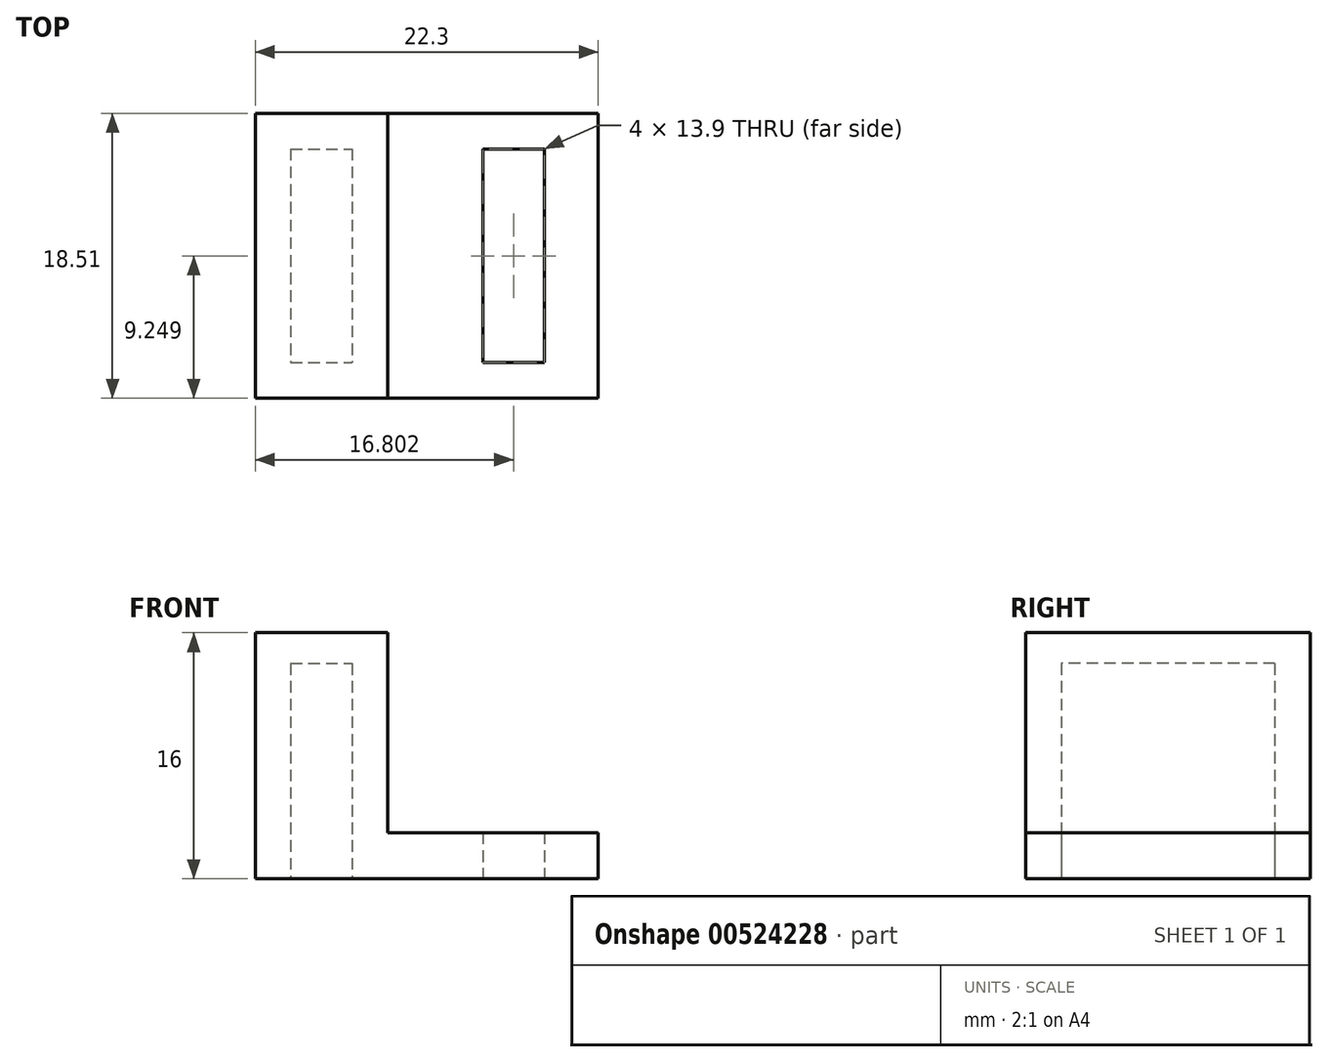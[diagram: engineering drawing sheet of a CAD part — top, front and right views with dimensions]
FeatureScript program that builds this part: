
annotation { "Feature Type Name" : "Feature", "Feature Type Description" : "" }
export const myFeature = defineFeature(function(context is Context, id is Id, definition is map)
    precondition{}
    {
        {
            var Q0;
            Q0=qCreatedBy(makeId("Top.planeOp"),FACE);
            var sketch = newSketch(context, id + "F0", { "sketchPlane" : qUnion([Q0])});
            skLineSegment(sketch, "E0.bottom", {"start": v(-48.96, 30.49) * mm, "end": v(-44.96, 30.49) * mm});
            skLineSegment(sketch, "E0.top", {"start": v(-48.96, 16.59) * mm, "end": v(-44.96, 16.59) * mm});
            skLineSegment(sketch, "E0.left", {"start": v(-48.96, 30.49) * mm, "end": v(-48.96, 16.59) * mm});
            skLineSegment(sketch, "E0.right", {"start": v(-44.96, 30.49) * mm, "end": v(-44.96, 16.59) * mm});
            skLineSegment(sketch, "E1", {"start": v(-44.96, 22.44) * mm, "end": v(-42.66, 22.44) * mm, "construction": true});
            skLineSegment(sketch, "E2", {"start": v(-42.66, 22.44) * mm, "end": v(-42.66, 42.18) * mm, "construction": true});
            skLineSegment(sketch, "E3", {"start": v(-42.66, 42.18) * mm, "end": v(-42.66, 0) * mm, "construction": true});
            skLineSegment(sketch, "E4", {"start": v(-46.96, 30.49) * mm, "end": v(-46.96, 32.79) * mm, "construction": true});
            skLineSegment(sketch, "E5", {"start": v(-46.96, 16.59) * mm, "end": v(-46.96, 14.29) * mm, "construction": true});
            skLineSegment(sketch, "E6", {"start": v(-42.66, 37.35) * mm, "end": v(-28.96, 37.35) * mm, "construction": true});
            skLineSegment(sketch, "E7", {"start": v(-28.96, 37.35) * mm, "end": v(-28.96, 6.43) * mm, "construction": true});
            skLineSegment(sketch, "E8", {"start": v(-46.96, 14.29) * mm, "end": v(-20.97, 14.29) * mm, "construction": true});
            skLineSegment(sketch, "E9", {"start": v(-48.96, 23.54) * mm, "end": v(-51.26, 23.54) * mm, "construction": true});
            skLineSegment(sketch, "E10", {"start": v(-51.26, 23.54) * mm, "end": v(-51.26, 42.06) * mm, "construction": true});
            skLineSegment(sketch, "E11", {"start": v(-51.26, 42.06) * mm, "end": v(-51.26, -3.78) * mm, "construction": true});
            skLineSegment(sketch, "E12", {"start": v(-46.96, 14.29) * mm, "end": v(-58.37, 14.29) * mm, "construction": true});
            skLineSegment(sketch, "E13.bottom", {"start": v(-51.26, 32.8) * mm, "end": v(-28.96, 32.8) * mm});
            skLineSegment(sketch, "E13.top", {"start": v(-51.26, 14.29) * mm, "end": v(-28.96, 14.29) * mm});
            skLineSegment(sketch, "E13.left", {"start": v(-51.26, 32.8) * mm, "end": v(-51.26, 14.29) * mm});
            skLineSegment(sketch, "E13.right", {"start": v(-28.96, 32.8) * mm, "end": v(-28.96, 14.29) * mm});
            skLineSegment(sketch, "E14", {"start": v(-44.96, 30.49) * mm, "end": v(-22.07, 30.49) * mm, "construction": true});
            skLineSegment(sketch, "E15", {"start": v(-44.96, 16.59) * mm, "end": v(-20.97, 16.59) * mm, "construction": true});
            skLineSegment(sketch, "E16", {"start": v(-28.96, 6.43) * mm, "end": v(-32.46, 6.43) * mm, "construction": true});
            skLineSegment(sketch, "E17", {"start": v(-32.46, 6.43) * mm, "end": v(-32.46, 38.78) * mm, "construction": true});
            skPoint(sketch, "E18.firstSnap0", {"position": v(-32.97, 16.59) * mm});
            skLineSegment(sketch, "E18.bottom", {"start": v(-32.46, 16.59) * mm, "end": v(-36.46, 16.59) * mm});
            skLineSegment(sketch, "E18.top", {"start": v(-32.46, 30.49) * mm, "end": v(-36.46, 30.49) * mm});
            skLineSegment(sketch, "E18.left", {"start": v(-32.46, 16.59) * mm, "end": v(-32.46, 30.49) * mm});
            skLineSegment(sketch, "E18.right", {"start": v(-36.46, 16.59) * mm, "end": v(-36.46, 30.49) * mm});
            skLineSegment(sketch, "E19", {"start": v(-42.66, 32.8) * mm, "end": v(-42.66, 14.29) * mm});
            skSolve(sketch);
        }
        {
            var Q0;
            Q0=makeQuery(id+"F0.imprint","IMPRINT",FACE,{"disambiguationData":[TD([[makeQuery(id+"F0.imprint","IMPRINT",EDGE,{"derivedFrom":sQuery(id+"F0.wireOp",EDGE,"E0.bottom")}),1.0]])]});
            extrude(context, id + "F1", {"entities" : qUnion([Q0]), "depth" : 14 * mm});
        }
        {
            var Q0;
            {var subQ0=sQuery(id+"F0.wireOp",EDGE,"E13.right");Q0=makeQuery(id+"F0.imprint","IMPRINT",FACE,{"disambiguationData":[TD([[makeQuery(id+"F0.imprint","IMPRINT",EDGE,{"derivedFrom":subQ0}),-1.0]])]});}
            extrude(context, id + "F2", {"entities" : qUnion([Q0]), "operationType" : NewBodyOperationType.ADD, "depth" : 3 * mm});
        }
        {
            var Q0;
            Q0=makeQuery(id+"F1.opExtrude","CAP_FACE",FACE,{"disambiguationData":[OSD([sQuery(id+"F0.wireOp",EDGE,"E0.bottom"),sQuery(id+"F0.wireOp",EDGE,"E0.top"),sQuery(id+"F0.wireOp",EDGE,"E0.left"),sQuery(id+"F0.wireOp",EDGE,"E0.right"),sQuery(id+"F0.wireOp",EDGE,"E13.bottom"),sQuery(id+"F0.wireOp",EDGE,"E13.top"),sQuery(id+"F0.wireOp",EDGE,"E13.left"),sQuery(id+"F0.wireOp",EDGE,"E19")])],"isStart":false});
            var sketch = newSketch(context, id + "F3", { "sketchPlane" : qUnion([Q0])});
            skLineSegment(sketch, "E20.bottom", {"start": v(-51.26, 32.8) * mm, "end": v(-42.66, 32.8) * mm});
            skLineSegment(sketch, "E20.top", {"start": v(-51.26, 14.29) * mm, "end": v(-42.66, 14.29) * mm});
            skLineSegment(sketch, "E20.left", {"start": v(-51.26, 32.8) * mm, "end": v(-51.26, 14.29) * mm});
            skLineSegment(sketch, "E20.right", {"start": v(-42.66, 32.8) * mm, "end": v(-42.66, 14.29) * mm});
            skSolve(sketch);
        }
        {
            var Q0;
            Q0=qSketchRegion(id+"F3",true);
            extrude(context, id + "F4", {"entities" : qUnion([Q0]), "operationType" : NewBodyOperationType.ADD, "depth" : 2 * mm});
        }
    });
